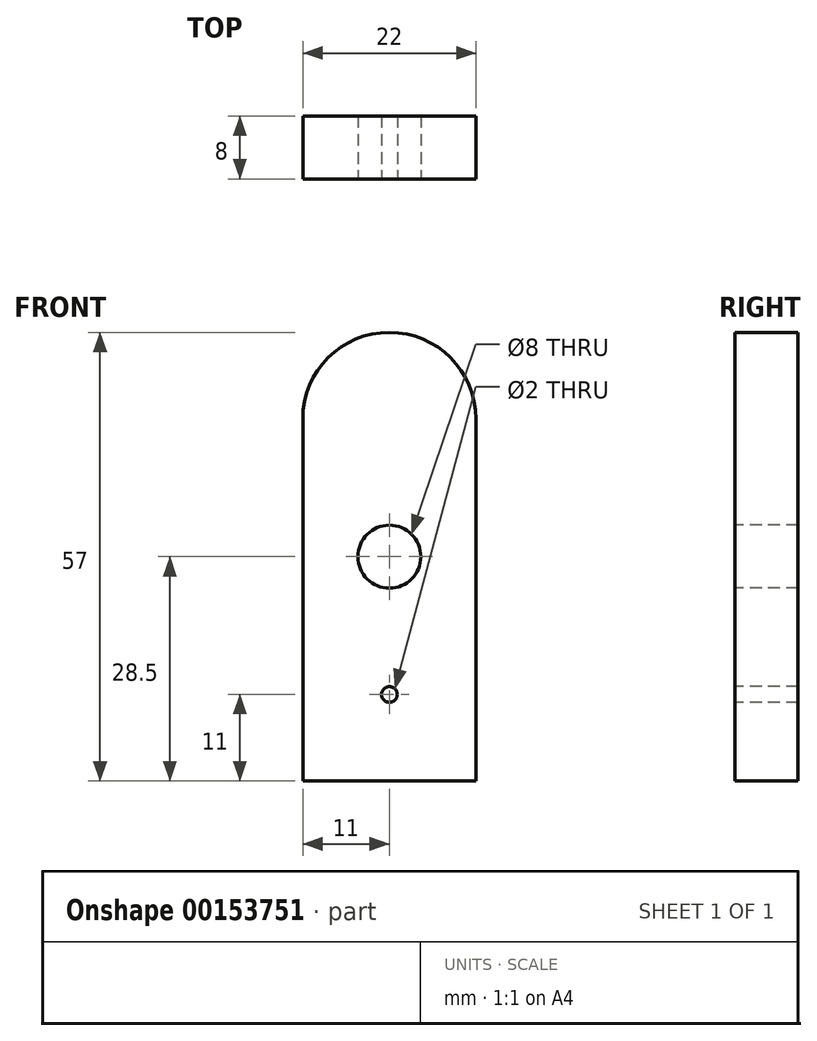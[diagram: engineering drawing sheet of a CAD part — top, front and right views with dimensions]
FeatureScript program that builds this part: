
annotation { "Feature Type Name" : "Feature", "Feature Type Description" : "" }
export const myFeature = defineFeature(function(context is Context, id is Id, definition is map)
    precondition{}
    {
        {
            var Q0;
            Q0=qCreatedBy(makeId("Front.planeOp"),FACE);
            var sketch = newSketch(context, id + "F0", { "sketchPlane" : qUnion([Q0])});
            skLineSegment(sketch, "E0.left", {"start": v(11, 17.5) * mm, "end": v(11, -17.5) * mm});
            skLineSegment(sketch, "E0.right", {"start": v(-11, 17.5) * mm, "end": v(-11, -17.5) * mm});
            skPoint(sketch, "E0.middle", {"position": v(0, 0) * mm});
            skCircle(sketch, "E1", {"center": v(0, 0) * mm, "radius": 4 * mm});
            skPoint(sketch, "E2.orphan", {"position": v(11, 30) * mm});
            skPoint(sketch, "E3.orphan", {"position": v(11, -27.63) * mm});
            skPoint(sketch, "E4.orphan", {"position": v(-11, -30) * mm});
            skPoint(sketch, "E5.visualSharp", {"position": v(-11, 33.5) * mm});
            skPoint(sketch, "E6.visualSharp", {"position": v(11, 33.5) * mm});
            skLineSegment(sketch, "E7", {"start": v(0, 17.5) * mm, "end": v(0, 18.42) * mm});
            skPoint(sketch, "E8.endSnap0", {"position": v(0, 26.5) * mm});
            skPoint(sketch, "E9.orphan", {"position": v(-11, 26.5) * mm});
            skPoint(sketch, "E10.orphan", {"position": v(11, 26.5) * mm});
            skLineSegment(sketch, "E11", {"start": v(-11, -17.5) * mm, "end": v(-11, -28.5) * mm});
            skLineSegment(sketch, "E12", {"start": v(11, -17.5) * mm, "end": v(11, -28.5) * mm});
            skLineSegment(sketch, "E13", {"start": v(0, -28.5) * mm, "end": v(11, -28.5) * mm});
            skLineSegment(sketch, "E14", {"start": v(0, -28.5) * mm, "end": v(-11, -28.5) * mm});
            skPoint(sketch, "E15.center.orphan", {"position": v(0, -17.5) * mm});
            skCircle(sketch, "E16", {"center": v(0, -17.5) * mm, "radius": 1 * mm});
            skArc(sketch, "E17", {"start": v(11, 17.5) * mm, "mid": v(0, 28.5) * mm, "end": v(-11, 17.5) * mm});
            skSolve(sketch);
        }
        {
            var Q0;
            Q0=makeQuery(id+"F0.imprint","IMPRINT",FACE,{"disambiguationData":[TD([[makeQuery(id+"F0.imprint","IMPRINT",EDGE,{"derivedFrom":sQuery(id+"F0.wireOp",EDGE,"E0.left")}),-1.0]])]});
            var Q1;
            {var subQ0=sQuery(id+"F0.wireOp",EDGE,"X2mgvhtn-K0Zp-JrRE-wkWX-ZBT09QaJ5OyT");Q1=makeQuery(id+"F0.imprint","IMPRINT",FACE,{"disambiguationData":[TD([[makeQuery(id+"F0.imprint","IMPRINT",EDGE,{"derivedFrom":subQ0}),1.0]])]});}
            var Q2;
            {var subQ0=sQuery(id+"F0.wireOp",EDGE,"w7UeX4FU-c1JB-PacW-90Tr-GThTYnYJkBC8");Q2=makeQuery(id+"F0.imprint","IMPRINT",FACE,{"disambiguationData":[TD([[makeQuery(id+"F0.imprint","IMPRINT",EDGE,{"derivedFrom":subQ0}),-1.0]])]});}
            var Q3;
            {var subQ1=sQuery(id+"F0.wireOp",EDGE,"jYNOUiBa-vmBM-d59c-WVce-bQadrZrCjrrx");Q3=makeQuery(id+"F0.imprint","IMPRINT",FACE,{"disambiguationData":[TD([[makeQuery(id+"F0.imprint","IMPRINT",EDGE,{"derivedFrom":subQ1}),1.0]])]});}
            extrude(context, id + "F1", {"entities" : qUnion([Q0, Q1, Q2, Q3]), "oppositeDirection" : true, "depth" : 8 * mm});
        }
    });
